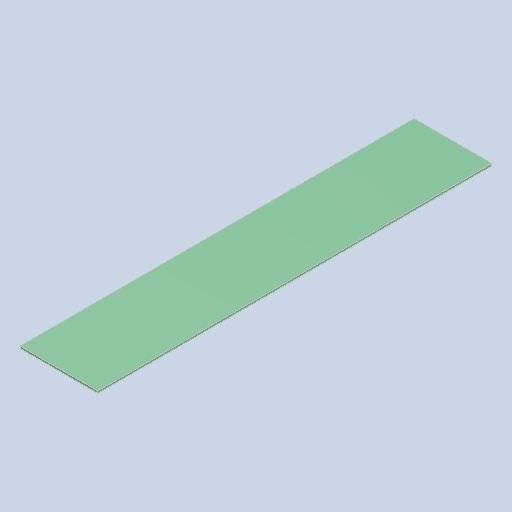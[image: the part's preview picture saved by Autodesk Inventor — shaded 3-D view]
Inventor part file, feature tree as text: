
AUTODESK INVENTOR PART (.ipt)
format: ipt  version: 2022 (Build 260153000, 153)  size: 94,720 bytes
history: native  units: mm
features: other x1, extrude x1, sketch x1
ambient origin geometry x8: Origin, YZ Plane, XZ Plane, XY Plane, X Axis, Y Axis, Z Axis, Center Point
bodies: Body1 (feature_tree)
feature tree (3):
  other  "ソリッド1"
  extrude  "押し出し1"  Depth=360.0mm
  sketch  "スケッチ1"
